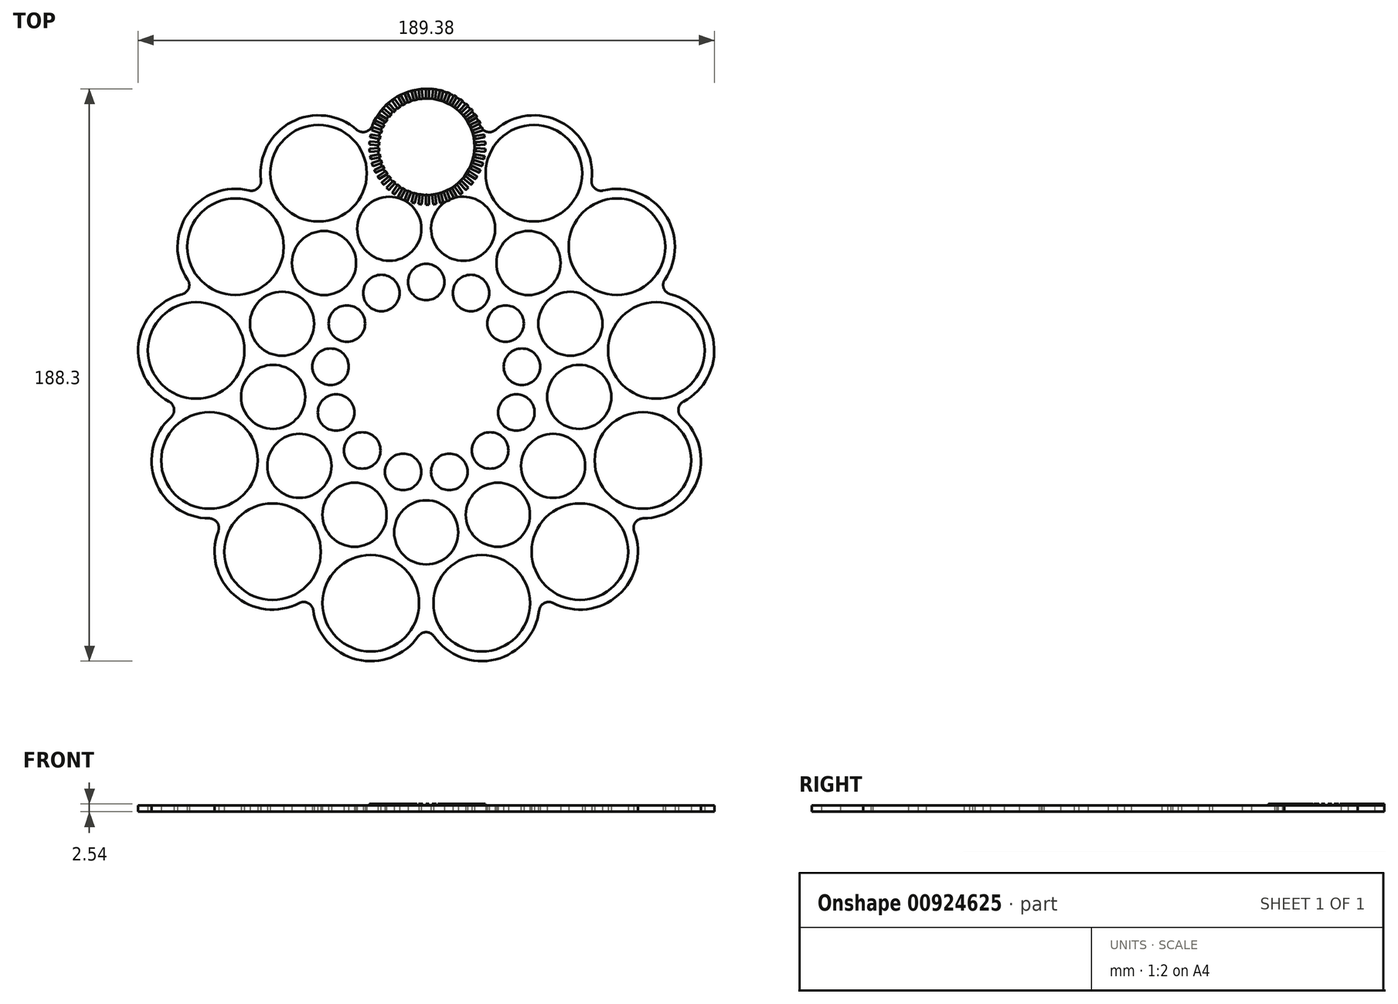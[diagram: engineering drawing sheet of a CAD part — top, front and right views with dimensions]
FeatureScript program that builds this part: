
annotation { "Feature Type Name" : "Feature", "Feature Type Description" : "" }
export const myFeature = defineFeature(function(context is Context, id is Id, definition is map)
    precondition{}
    {
        {
            var Q0;
            Q0=qCreatedBy(makeId("Top.planeOp"),FACE);
            var sketch = newSketch(context, id + "F0", { "sketchPlane" : qUnion([Q0])});
            skLineSegment(sketch, "E0", {"start": v(0, 0) * mm, "end": v(0, 76.2) * mm, "construction": true});
            skCircle(sketch, "E1", {"center": v(0, 76.2) * mm, "radius": 15.88 * mm});
            skLineSegment(sketch, "E2", {"start": v(0, 95.25) * mm, "end": v(0, 15.88) * mm, "construction": true});
            skCircle(sketch, "E3.1.0", {"center": v(-35.41, 67.47) * mm, "radius": 15.88 * mm});
            skArc(sketch, "E3.1.1", {"start": v(-22.84, 81.79) * mm, "mid": v(-44.26, 84.34) * mm, "end": v(-54.33, 65.26) * mm});
            skCircle(sketch, "E3.2.0", {"center": v(-62.71, 43.29) * mm, "radius": 15.88 * mm});
            skArc(sketch, "E3.2.1", {"start": v(-58.23, 61.8) * mm, "mid": v(-78.39, 54.1) * mm, "end": v(-78.44, 32.53) * mm});
            skCircle(sketch, "E3.3.0", {"center": v(-75.64, 9.18) * mm, "radius": 15.88 * mm});
            skArc(sketch, "E3.3.1", {"start": v(-80.28, 27.66) * mm, "mid": v(-94.56, 11.48) * mm, "end": v(-84.57, -7.64) * mm});
            skCircle(sketch, "E3.4.0", {"center": v(-71.25, -27.02) * mm, "radius": 15.88 * mm});
            skArc(sketch, "E3.4.1", {"start": v(-83.94, -12.82) * mm, "mid": v(-89.06, -33.78) * mm, "end": v(-71.33, -46.07) * mm});
            skCircle(sketch, "E3.5.0", {"center": v(-50.53, -57.04) * mm, "radius": 15.88 * mm});
            skArc(sketch, "E3.5.1", {"start": v(-68.37, -50.36) * mm, "mid": v(-63.16, -71.3) * mm, "end": v(-41.75, -73.94) * mm});
            skCircle(sketch, "E3.6.0", {"center": v(-18.24, -73.99) * mm, "radius": 15.88 * mm});
            skArc(sketch, "E3.6.1", {"start": v(-37.14, -76.36) * mm, "mid": v(-22.8, -92.48) * mm, "end": v(-2.6, -84.88) * mm});
            skCircle(sketch, "E3.7.0", {"center": v(18.24, -73.99) * mm, "radius": 15.88 * mm});
            skArc(sketch, "E3.7.1", {"start": v(2.6, -84.88) * mm, "mid": v(22.8, -92.48) * mm, "end": v(37.14, -76.36) * mm});
            skCircle(sketch, "E3.8.0", {"center": v(50.53, -57.04) * mm, "radius": 15.88 * mm});
            skArc(sketch, "E3.8.1", {"start": v(41.75, -73.94) * mm, "mid": v(63.16, -71.3) * mm, "end": v(68.37, -50.36) * mm});
            skCircle(sketch, "E3.9.0", {"center": v(71.25, -27.02) * mm, "radius": 15.88 * mm});
            skCircle(sketch, "E3.10.0", {"center": v(75.64, 9.18) * mm, "radius": 15.88 * mm});
            skArc(sketch, "E3.10.1", {"start": v(84.57, -7.64) * mm, "mid": v(94.56, 11.48) * mm, "end": v(80.28, 27.66) * mm});
            skCircle(sketch, "E3.11.0", {"center": v(62.71, 43.29) * mm, "radius": 15.88 * mm});
            skArc(sketch, "E3.11.1", {"start": v(78.44, 32.53) * mm, "mid": v(78.39, 54.1) * mm, "end": v(58.23, 61.8) * mm});
            skCircle(sketch, "E3.12.0", {"center": v(35.41, 67.47) * mm, "radius": 15.88 * mm});
            skPoint(sketch, "E3.center", {"position": v(0, 0) * mm});
            skLineSegment(sketch, "E4", {"start": v(0, 0) * mm, "end": v(35.41, 67.47) * mm, "construction": true});
            skLineSegment(sketch, "E5.0", {"start": v(-1.59, 0) * mm, "end": v(-1.59, 76.2) * mm, "construction": true});
            skLineSegment(sketch, "E6.0", {"start": v(1.4, -0.74) * mm, "end": v(36.82, 66.73) * mm, "construction": true});
            skCircle(sketch, "E7.0", {"center": v(12.13, 49.2) * mm, "radius": 10.54 * mm});
            skCircle(sketch, "E8.1.0", {"center": v(-12.13, 49.2) * mm, "radius": 10.54 * mm});
            skCircle(sketch, "E8.2.0", {"center": v(-33.6, 37.94) * mm, "radius": 10.54 * mm});
            skCircle(sketch, "E8.3.0", {"center": v(-47.39, 17.97) * mm, "radius": 10.54 * mm});
            skCircle(sketch, "E8.4.0", {"center": v(-50.31, -6.1) * mm, "radius": 10.54 * mm});
            skCircle(sketch, "E8.5.0", {"center": v(-41.7, -28.8) * mm, "radius": 10.54 * mm});
            skCircle(sketch, "E8.6.0", {"center": v(-23.55, -44.88) * mm, "radius": 10.54 * mm});
            skCircle(sketch, "E8.7.0", {"center": v(0, -50.68) * mm, "radius": 10.54 * mm});
            skCircle(sketch, "E8.8.0", {"center": v(23.55, -44.88) * mm, "radius": 10.54 * mm});
            skCircle(sketch, "E8.9.0", {"center": v(41.7, -28.8) * mm, "radius": 10.54 * mm});
            skCircle(sketch, "E8.10.0", {"center": v(50.31, -6.1) * mm, "radius": 10.54 * mm});
            skCircle(sketch, "E8.11.0", {"center": v(47.39, 17.97) * mm, "radius": 10.54 * mm});
            skCircle(sketch, "E8.12.0", {"center": v(33.6, 37.94) * mm, "radius": 10.54 * mm});
            skLineSegment(sketch, "E9", {"start": v(12.13, 49.2) * mm, "end": v(0, 0) * mm, "construction": true});
            skArc(sketch, "E10.trimOffspring", {"start": v(17.78, 83.03) * mm, "mid": v(0, 95.25) * mm, "end": v(-17.78, 83.03) * mm});
            skArc(sketch, "E11.trimOffspring", {"start": v(54.33, 65.26) * mm, "mid": v(44.26, 84.34) * mm, "end": v(22.84, 81.79) * mm});
            skCircle(sketch, "E12.0", {"center": v(0, 31.7) * mm, "radius": 6 * mm});
            skCircle(sketch, "E13.1.0", {"center": v(-14.73, 28.07) * mm, "radius": 6 * mm});
            skCircle(sketch, "E13.2.0", {"center": v(-26.09, 18) * mm, "radius": 6 * mm});
            skCircle(sketch, "E13.3.0", {"center": v(-31.47, 3.82) * mm, "radius": 6 * mm});
            skCircle(sketch, "E13.4.0", {"center": v(-29.64, -11.24) * mm, "radius": 6 * mm});
            skCircle(sketch, "E13.5.0", {"center": v(-21.02, -23.73) * mm, "radius": 6 * mm});
            skCircle(sketch, "E13.6.0", {"center": v(-7.59, -30.78) * mm, "radius": 6 * mm});
            skCircle(sketch, "E13.7.0", {"center": v(7.59, -30.78) * mm, "radius": 6 * mm});
            skCircle(sketch, "E13.8.0", {"center": v(21.02, -23.73) * mm, "radius": 6 * mm});
            skCircle(sketch, "E13.9.0", {"center": v(29.64, -11.24) * mm, "radius": 6 * mm});
            skCircle(sketch, "E13.10.0", {"center": v(31.47, 3.82) * mm, "radius": 6 * mm});
            skCircle(sketch, "E13.11.0", {"center": v(26.09, 18) * mm, "radius": 6 * mm});
            skCircle(sketch, "E13.12.0", {"center": v(14.73, 28.07) * mm, "radius": 6 * mm});
            skArc(sketch, "E14.trimOffspring", {"start": v(71.33, -46.07) * mm, "mid": v(89.06, -33.78) * mm, "end": v(83.94, -12.82) * mm});
            skPoint(sketch, "E15.visualSharp", {"position": v(-52.72, 59.5) * mm});
            skArc(sketch, "E15.filletArc", {"start": v(-58.23, 61.8) * mm, "mid": v(-55.38, 62.51) * mm, "end": v(-54.33, 65.26) * mm});
            skPoint(sketch, "E16.visualSharp", {"position": v(-74.33, 28.19) * mm});
            skArc(sketch, "E16.filletArc", {"start": v(-80.28, 27.66) * mm, "mid": v(-78.09, 29.61) * mm, "end": v(-78.44, 32.53) * mm});
            skPoint(sketch, "E17.visualSharp", {"position": v(-78.92, -9.58) * mm});
            skArc(sketch, "E17.filletArc", {"start": v(-83.94, -12.82) * mm, "mid": v(-82.9, -10.07) * mm, "end": v(-84.57, -7.64) * mm});
            skPoint(sketch, "E18.visualSharp", {"position": v(-65.42, -45.16) * mm});
            skArc(sketch, "E18.filletArc", {"start": v(-68.37, -50.36) * mm, "mid": v(-68.73, -47.44) * mm, "end": v(-71.33, -46.07) * mm});
            skPoint(sketch, "E19.visualSharp", {"position": v(-36.94, -70.39) * mm});
            skArc(sketch, "E19.filletArc", {"start": v(-37.14, -76.36) * mm, "mid": v(-38.81, -73.95) * mm, "end": v(-41.75, -73.94) * mm});
            skPoint(sketch, "E20.visualSharp", {"position": v(0, -79.5) * mm});
            skArc(sketch, "E20.filletArc", {"start": v(2.6, -84.88) * mm, "mid": v(0, -83.52) * mm, "end": v(-2.6, -84.88) * mm});
            skPoint(sketch, "E21.visualSharp", {"position": v(36.94, -70.39) * mm});
            skArc(sketch, "E21.filletArc", {"start": v(41.75, -73.94) * mm, "mid": v(38.81, -73.95) * mm, "end": v(37.14, -76.36) * mm});
            skPoint(sketch, "E22.visualSharp", {"position": v(65.42, -45.16) * mm});
            skArc(sketch, "E22.filletArc", {"start": v(71.33, -46.07) * mm, "mid": v(68.73, -47.44) * mm, "end": v(68.37, -50.36) * mm});
            skPoint(sketch, "E23.visualSharp", {"position": v(78.92, -9.58) * mm});
            skArc(sketch, "E23.filletArc", {"start": v(84.57, -7.64) * mm, "mid": v(82.9, -10.07) * mm, "end": v(83.94, -12.82) * mm});
            skPoint(sketch, "E24.visualSharp", {"position": v(74.33, 28.19) * mm});
            skArc(sketch, "E24.filletArc", {"start": v(78.44, 32.53) * mm, "mid": v(78.09, 29.61) * mm, "end": v(80.28, 27.66) * mm});
            skPoint(sketch, "E25.visualSharp", {"position": v(52.72, 59.5) * mm});
            skArc(sketch, "E25.filletArc", {"start": v(54.33, 65.26) * mm, "mid": v(55.38, 62.51) * mm, "end": v(58.23, 61.8) * mm});
            skPoint(sketch, "E26.visualSharp", {"position": v(19.02, 77.19) * mm});
            skArc(sketch, "E26.filletArc", {"start": v(17.78, 83.03) * mm, "mid": v(19.99, 81.09) * mm, "end": v(22.84, 81.79) * mm});
            skPoint(sketch, "E27.visualSharp", {"position": v(-19.02, 77.19) * mm});
            skArc(sketch, "E27.filletArc", {"start": v(-22.84, 81.79) * mm, "mid": v(-19.99, 81.09) * mm, "end": v(-17.78, 83.03) * mm});
            skSolve(sketch);
        }
        {
            var Q0;
            Q0 = qSketchRegion(id + "F0", true);
            extrude(context, id + "F1", {"entities" : qUnion([Q0]), "depth" : 2.03 * mm, "offsetDistance" : 25.4 * mm});
        }
        {
            var Q0;
            Q0=makeQuery(id+"F1.opExtrude","CAP_FACE",FACE,{"disambiguationData":[OSD([sQuery(id+"F0.wireOp",EDGE,"PSAwym5H-QxkA-4yG9-N3LV-itEtamM54euJ"),sQuery(id+"F0.wireOp",EDGE,"xVTmrC7g-0ckz-Fa8x-Pjiv-ewgNsUpUR1TQ"),sQuery(id+"F0.wireOp",EDGE,"E1"),sQuery(id+"F0.wireOp",EDGE,"fK0bV1JR-EDHa-cPX2-9ya8-nsOdXMEwq4Jo"),sQuery(id+"F0.wireOp",EDGE,"c6219e1f-16d4-4bd9-93b5-d01c4ede8f85"),sQuery(id+"F0.wireOp",EDGE,"f72ceaee-ed20-4dc2-a844-dc1204d0d60d.trimOffspring"),sQuery(id+"F0.wireOp",EDGE,"bad8b10d-c7dc-4f17-be22-73a892854aa8.trimOffspring"),sQuery(id+"F0.wireOp",EDGE,"7017c75f-0572-4b0f-bba0-e0d1ac50efab.trimOffspring"),sQuery(id+"F0.wireOp",EDGE,"a2bf4c4b-1b04-41ae-a137-ce36847d082b.filletArc"),sQuery(id+"F0.wireOp",EDGE,"9a5818be-14a7-4684-8801-1bcc1c34eb4a.filletArc"),sQuery(id+"F0.wireOp",EDGE,"76f430f3-cf00-46af-aaf1-ca3324483fb8.filletArc"),sQuery(id+"F0.wireOp",EDGE,"f2824564-7fb7-4ffd-9573-8c77cc779830.filletArc"),sQuery(id+"F0.wireOp",EDGE,"6882c2d4-6085-444e-aa9e-9cba060f5f8f.filletArc"),sQuery(id+"F0.wireOp",EDGE,"d489b73e-8a5e-456b-afac-9e78a89a280e.filletArc"),sQuery(id+"F0.wireOp",EDGE,"7932d08e-b7d8-4a8b-9c19-5e9f429760f1.trimOffspring"),sQuery(id+"F0.wireOp",EDGE,"vGADDeQr-Uufc-AQag-ZwEX-BwhNSN2T0gA2"),sQuery(id+"F0.wireOp",EDGE,"5JA08mAS-do2W-TdYA-RMZA-uYhekkPeP3UP")])],"isStart":false});
            var sketch = newSketch(context, id + "F2", { "sketchPlane" : qUnion([Q0])});
            skLineSegment(sketch, "E28", {"start": v(0.39, 95.26) * mm, "end": v(0.39, 92.07) * mm, "construction": true});
            skLineSegment(sketch, "E29.0", {"start": v(-0.12, 95.26) * mm, "end": v(-0.12, 92.07) * mm});
            skLineSegment(sketch, "E30", {"start": v(0.9, 95.25) * mm, "end": v(0.9, 92.05) * mm});
            skArc(sketch, "E31.0", {"start": v(0.9, 95.25) * mm, "mid": v(0.39, 95.26) * mm, "end": v(-0.12, 95.25) * mm});
            skArc(sketch, "E32.0", {"start": v(0.9, 92.05) * mm, "mid": v(0.39, 92.07) * mm, "end": v(-0.12, 92.07) * mm});
            skPoint(sketch, "E33.orphan", {"position": v(-12.06, 61.79) * mm});
            skPoint(sketch, "E34.orphan", {"position": v(12.84, 61.79) * mm});
            skLineSegment(sketch, "E35.1.0", {"start": v(-2.5, 95.04) * mm, "end": v(-2.1, 91.89) * mm});
            skLineSegment(sketch, "E35.1.1", {"start": v(-1.5, 95.16) * mm, "end": v(-1.1, 91.99) * mm});
            skLineSegment(sketch, "E35.1.2", {"start": v(-2, 95.1) * mm, "end": v(-1.6, 91.95) * mm, "construction": true});
            skArc(sketch, "E35.1.3", {"start": v(-1.1, 91.99) * mm, "mid": v(-1.6, 91.95) * mm, "end": v(-2.1, 91.89) * mm});
            skArc(sketch, "E35.1.4", {"start": v(-1.5, 95.16) * mm, "mid": v(-2, 95.1) * mm, "end": v(-2.5, 95.04) * mm});
            skLineSegment(sketch, "E35.2.0", {"start": v(-4.84, 94.53) * mm, "end": v(-4.05, 91.45) * mm});
            skLineSegment(sketch, "E35.2.1", {"start": v(-3.86, 94.78) * mm, "end": v(-3.06, 91.68) * mm});
            skLineSegment(sketch, "E35.2.2", {"start": v(-4.35, 94.66) * mm, "end": v(-3.56, 91.57) * mm, "construction": true});
            skArc(sketch, "E35.2.3", {"start": v(-3.06, 91.68) * mm, "mid": v(-3.56, 91.57) * mm, "end": v(-4.05, 91.45) * mm});
            skArc(sketch, "E35.2.4", {"start": v(-3.86, 94.78) * mm, "mid": v(-4.35, 94.66) * mm, "end": v(-4.84, 94.53) * mm});
            skLineSegment(sketch, "E35.3.0", {"start": v(-7.1, 93.73) * mm, "end": v(-5.93, 90.77) * mm});
            skLineSegment(sketch, "E35.3.1", {"start": v(-6.15, 94.1) * mm, "end": v(-4.97, 91.12) * mm});
            skLineSegment(sketch, "E35.3.2", {"start": v(-6.63, 93.92) * mm, "end": v(-5.45, 90.96) * mm, "construction": true});
            skArc(sketch, "E35.3.3", {"start": v(-4.97, 91.12) * mm, "mid": v(-5.45, 90.96) * mm, "end": v(-5.93, 90.77) * mm});
            skArc(sketch, "E35.3.4", {"start": v(-6.15, 94.1) * mm, "mid": v(-6.63, 93.92) * mm, "end": v(-7.1, 93.73) * mm});
            skLineSegment(sketch, "E35.4.0", {"start": v(-9.24, 92.66) * mm, "end": v(-7.7, 89.87) * mm});
            skLineSegment(sketch, "E35.4.1", {"start": v(-8.34, 93.14) * mm, "end": v(-6.8, 90.33) * mm});
            skLineSegment(sketch, "E35.4.2", {"start": v(-8.8, 92.9) * mm, "end": v(-7.25, 90.1) * mm, "construction": true});
            skArc(sketch, "E35.4.3", {"start": v(-6.8, 90.33) * mm, "mid": v(-7.25, 90.1) * mm, "end": v(-7.7, 89.87) * mm});
            skArc(sketch, "E35.4.4", {"start": v(-8.34, 93.14) * mm, "mid": v(-8.8, 92.9) * mm, "end": v(-9.23, 92.65) * mm});
            skLineSegment(sketch, "E35.5.0", {"start": v(-11.22, 91.32) * mm, "end": v(-9.35, 88.75) * mm});
            skLineSegment(sketch, "E35.5.1", {"start": v(-10.4, 91.91) * mm, "end": v(-8.51, 89.32) * mm});
            skLineSegment(sketch, "E35.5.2", {"start": v(-10.81, 91.62) * mm, "end": v(-8.94, 89.04) * mm, "construction": true});
            skArc(sketch, "E35.5.3", {"start": v(-8.51, 89.32) * mm, "mid": v(-8.94, 89.04) * mm, "end": v(-9.35, 88.75) * mm});
            skArc(sketch, "E35.5.4", {"start": v(-10.4, 91.91) * mm, "mid": v(-10.81, 91.62) * mm, "end": v(-11.22, 91.32) * mm});
            skLineSegment(sketch, "E35.6.0", {"start": v(-13.02, 89.75) * mm, "end": v(-10.84, 87.43) * mm});
            skLineSegment(sketch, "E35.6.1", {"start": v(-12.28, 90.44) * mm, "end": v(-10.09, 88.1) * mm});
            skLineSegment(sketch, "E35.6.2", {"start": v(-12.65, 90.1) * mm, "end": v(-10.47, 87.77) * mm, "construction": true});
            skArc(sketch, "E35.6.3", {"start": v(-10.09, 88.1) * mm, "mid": v(-10.47, 87.77) * mm, "end": v(-10.84, 87.43) * mm});
            skArc(sketch, "E35.6.4", {"start": v(-12.28, 90.44) * mm, "mid": v(-12.65, 90.1) * mm, "end": v(-13.02, 89.74) * mm});
            skLineSegment(sketch, "E35.7.0", {"start": v(-14.62, 87.96) * mm, "end": v(-12.16, 85.93) * mm});
            skLineSegment(sketch, "E35.7.1", {"start": v(-13.96, 88.74) * mm, "end": v(-11.5, 86.7) * mm});
            skLineSegment(sketch, "E35.7.2", {"start": v(-14.3, 88.35) * mm, "end": v(-11.84, 86.32) * mm, "construction": true});
            skArc(sketch, "E35.7.3", {"start": v(-11.5, 86.7) * mm, "mid": v(-11.84, 86.32) * mm, "end": v(-12.16, 85.93) * mm});
            skArc(sketch, "E35.7.4", {"start": v(-13.96, 88.74) * mm, "mid": v(-14.3, 88.35) * mm, "end": v(-14.6, 87.95) * mm});
            skLineSegment(sketch, "E35.8.0", {"start": v(-15.97, 85.99) * mm, "end": v(-13.28, 84.28) * mm});
            skLineSegment(sketch, "E35.8.1", {"start": v(-15.42, 86.84) * mm, "end": v(-12.72, 85.13) * mm});
            skLineSegment(sketch, "E35.8.2", {"start": v(-15.7, 86.42) * mm, "end": v(-13, 84.7) * mm, "construction": true});
            skArc(sketch, "E35.8.3", {"start": v(-12.72, 85.13) * mm, "mid": v(-13, 84.7) * mm, "end": v(-13.28, 84.28) * mm});
            skArc(sketch, "E35.8.4", {"start": v(-15.42, 86.84) * mm, "mid": v(-15.7, 86.42) * mm, "end": v(-15.96, 85.98) * mm});
            skLineSegment(sketch, "E35.9.0", {"start": v(-17.07, 83.86) * mm, "end": v(-14.19, 82.5) * mm});
            skLineSegment(sketch, "E35.9.1", {"start": v(-16.63, 84.78) * mm, "end": v(-13.73, 83.41) * mm});
            skLineSegment(sketch, "E35.9.2", {"start": v(-16.85, 84.32) * mm, "end": v(-13.97, 82.96) * mm, "construction": true});
            skArc(sketch, "E35.9.3", {"start": v(-13.73, 83.41) * mm, "mid": v(-13.97, 82.96) * mm, "end": v(-14.19, 82.5) * mm});
            skArc(sketch, "E35.9.4", {"start": v(-16.63, 84.78) * mm, "mid": v(-16.85, 84.32) * mm, "end": v(-17.06, 83.86) * mm});
            skLineSegment(sketch, "E35.10.0", {"start": v(-17.89, 81.61) * mm, "end": v(-14.86, 80.63) * mm});
            skLineSegment(sketch, "E35.10.1", {"start": v(-17.57, 82.58) * mm, "end": v(-14.52, 81.59) * mm});
            skLineSegment(sketch, "E35.10.2", {"start": v(-17.73, 82.1) * mm, "end": v(-14.7, 81.1) * mm, "construction": true});
            skArc(sketch, "E35.10.3", {"start": v(-14.52, 81.59) * mm, "mid": v(-14.7, 81.1) * mm, "end": v(-14.86, 80.63) * mm});
            skArc(sketch, "E35.10.4", {"start": v(-17.57, 82.58) * mm, "mid": v(-17.73, 82.1) * mm, "end": v(-17.88, 81.6) * mm});
            skLineSegment(sketch, "E35.11.0", {"start": v(-18.42, 79.28) * mm, "end": v(-15.3, 78.68) * mm});
            skLineSegment(sketch, "E35.11.1", {"start": v(-18.22, 80.28) * mm, "end": v(-15.08, 79.68) * mm});
            skLineSegment(sketch, "E35.11.2", {"start": v(-18.33, 79.78) * mm, "end": v(-15.2, 79.18) * mm, "construction": true});
            skArc(sketch, "E35.11.3", {"start": v(-15.08, 79.68) * mm, "mid": v(-15.2, 79.18) * mm, "end": v(-15.3, 78.68) * mm});
            skArc(sketch, "E35.11.4", {"start": v(-18.22, 80.28) * mm, "mid": v(-18.33, 79.78) * mm, "end": v(-18.41, 79.28) * mm});
            skLineSegment(sketch, "E35.12.0", {"start": v(-18.66, 76.9) * mm, "end": v(-15.48, 76.7) * mm});
            skLineSegment(sketch, "E35.12.1", {"start": v(-18.59, 77.91) * mm, "end": v(-15.4, 77.7) * mm});
            skLineSegment(sketch, "E35.12.2", {"start": v(-18.63, 77.4) * mm, "end": v(-15.44, 77.2) * mm, "construction": true});
            skArc(sketch, "E35.12.3", {"start": v(-15.4, 77.7) * mm, "mid": v(-15.44, 77.2) * mm, "end": v(-15.48, 76.7) * mm});
            skArc(sketch, "E35.12.4", {"start": v(-18.59, 77.91) * mm, "mid": v(-18.63, 77.4) * mm, "end": v(-18.65, 76.9) * mm});
            skLineSegment(sketch, "E35.13.0", {"start": v(-18.6, 74.5) * mm, "end": v(-15.42, 74.7) * mm});
            skLineSegment(sketch, "E35.13.1", {"start": v(-18.65, 75.52) * mm, "end": v(-15.46, 75.72) * mm});
            skLineSegment(sketch, "E35.13.2", {"start": v(-18.63, 75.01) * mm, "end": v(-15.44, 75.21) * mm, "construction": true});
            skArc(sketch, "E35.13.3", {"start": v(-15.46, 75.72) * mm, "mid": v(-15.44, 75.21) * mm, "end": v(-15.42, 74.7) * mm});
            skArc(sketch, "E35.13.4", {"start": v(-18.65, 75.52) * mm, "mid": v(-18.63, 75.01) * mm, "end": v(-18.59, 74.5) * mm});
            skLineSegment(sketch, "E35.14.0", {"start": v(-18.23, 72.14) * mm, "end": v(-15.1, 72.74) * mm});
            skLineSegment(sketch, "E35.14.1", {"start": v(-18.41, 73.14) * mm, "end": v(-15.27, 73.74) * mm});
            skLineSegment(sketch, "E35.14.2", {"start": v(-18.33, 72.64) * mm, "end": v(-15.2, 73.24) * mm, "construction": true});
            skArc(sketch, "E35.14.3", {"start": v(-15.27, 73.74) * mm, "mid": v(-15.2, 73.24) * mm, "end": v(-15.1, 72.74) * mm});
            skArc(sketch, "E35.14.4", {"start": v(-18.41, 73.14) * mm, "mid": v(-18.33, 72.64) * mm, "end": v(-18.22, 72.14) * mm});
            skLineSegment(sketch, "E35.15.0", {"start": v(-17.57, 69.84) * mm, "end": v(-14.55, 70.82) * mm});
            skLineSegment(sketch, "E35.15.1", {"start": v(-17.88, 70.8) * mm, "end": v(-14.84, 71.8) * mm});
            skLineSegment(sketch, "E35.15.2", {"start": v(-17.73, 70.32) * mm, "end": v(-14.7, 71.3) * mm, "construction": true});
            skArc(sketch, "E35.15.3", {"start": v(-14.84, 71.8) * mm, "mid": v(-14.7, 71.3) * mm, "end": v(-14.55, 70.82) * mm});
            skArc(sketch, "E35.15.4", {"start": v(-17.88, 70.8) * mm, "mid": v(-17.73, 70.32) * mm, "end": v(-17.57, 69.84) * mm});
            skLineSegment(sketch, "E35.16.0", {"start": v(-16.63, 67.64) * mm, "end": v(-13.75, 69) * mm});
            skLineSegment(sketch, "E35.16.1", {"start": v(-17.06, 68.56) * mm, "end": v(-14.16, 69.92) * mm});
            skLineSegment(sketch, "E35.16.2", {"start": v(-16.85, 68.1) * mm, "end": v(-13.97, 69.45) * mm, "construction": true});
            skArc(sketch, "E35.16.3", {"start": v(-14.16, 69.92) * mm, "mid": v(-13.97, 69.45) * mm, "end": v(-13.75, 69) * mm});
            skArc(sketch, "E35.16.4", {"start": v(-17.06, 68.56) * mm, "mid": v(-16.85, 68.1) * mm, "end": v(-16.63, 67.64) * mm});
            skLineSegment(sketch, "E35.17.0", {"start": v(-15.43, 65.57) * mm, "end": v(-12.74, 67.28) * mm});
            skLineSegment(sketch, "E35.17.1", {"start": v(-15.96, 66.43) * mm, "end": v(-13.26, 68.15) * mm});
            skLineSegment(sketch, "E35.17.2", {"start": v(-15.7, 66) * mm, "end": v(-13, 67.7) * mm, "construction": true});
            skArc(sketch, "E35.17.3", {"start": v(-13.26, 68.15) * mm, "mid": v(-13, 67.7) * mm, "end": v(-12.74, 67.28) * mm});
            skArc(sketch, "E35.17.4", {"start": v(-15.96, 66.43) * mm, "mid": v(-15.7, 66) * mm, "end": v(-15.42, 65.57) * mm});
            skLineSegment(sketch, "E35.18.0", {"start": v(-13.97, 63.67) * mm, "end": v(-11.51, 65.7) * mm});
            skLineSegment(sketch, "E35.18.1", {"start": v(-14.6, 64.46) * mm, "end": v(-12.14, 66.5) * mm});
            skLineSegment(sketch, "E35.18.2", {"start": v(-14.3, 64.06) * mm, "end": v(-11.84, 66.1) * mm, "construction": true});
            skArc(sketch, "E35.18.3", {"start": v(-12.14, 66.5) * mm, "mid": v(-11.84, 66.1) * mm, "end": v(-11.51, 65.7) * mm});
            skArc(sketch, "E35.18.4", {"start": v(-14.6, 64.46) * mm, "mid": v(-14.3, 64.06) * mm, "end": v(-13.96, 63.68) * mm});
            skLineSegment(sketch, "E35.19.0", {"start": v(-12.28, 61.97) * mm, "end": v(-10.1, 64.3) * mm});
            skLineSegment(sketch, "E35.19.1", {"start": v(-13.02, 62.67) * mm, "end": v(-10.83, 65) * mm});
            skLineSegment(sketch, "E35.19.2", {"start": v(-12.65, 62.32) * mm, "end": v(-10.47, 64.64) * mm, "construction": true});
            skArc(sketch, "E35.19.3", {"start": v(-10.83, 65) * mm, "mid": v(-10.47, 64.64) * mm, "end": v(-10.1, 64.3) * mm});
            skArc(sketch, "E35.19.4", {"start": v(-13.02, 62.67) * mm, "mid": v(-12.65, 62.32) * mm, "end": v(-12.28, 61.98) * mm});
            skLineSegment(sketch, "E35.20.0", {"start": v(-10.4, 60.5) * mm, "end": v(-8.53, 63.07) * mm});
            skLineSegment(sketch, "E35.20.1", {"start": v(-11.22, 61.1) * mm, "end": v(-9.34, 63.69) * mm});
            skLineSegment(sketch, "E35.20.2", {"start": v(-10.81, 60.8) * mm, "end": v(-8.94, 63.37) * mm, "construction": true});
            skArc(sketch, "E35.20.3", {"start": v(-9.34, 63.69) * mm, "mid": v(-8.94, 63.37) * mm, "end": v(-8.53, 63.07) * mm});
            skArc(sketch, "E35.20.4", {"start": v(-11.22, 61.1) * mm, "mid": v(-10.81, 60.8) * mm, "end": v(-10.4, 60.5) * mm});
            skLineSegment(sketch, "E35.21.0", {"start": v(-8.35, 59.27) * mm, "end": v(-6.81, 62.06) * mm});
            skLineSegment(sketch, "E35.21.1", {"start": v(-9.23, 59.76) * mm, "end": v(-7.7, 62.57) * mm});
            skLineSegment(sketch, "E35.21.2", {"start": v(-8.8, 59.51) * mm, "end": v(-7.25, 62.3) * mm, "construction": true});
            skArc(sketch, "E35.21.3", {"start": v(-7.7, 62.57) * mm, "mid": v(-7.26, 62.3) * mm, "end": v(-6.81, 62.06) * mm});
            skArc(sketch, "E35.21.4", {"start": v(-9.23, 59.76) * mm, "mid": v(-8.8, 59.51) * mm, "end": v(-8.34, 59.28) * mm});
            skLineSegment(sketch, "E35.22.0", {"start": v(-6.15, 58.3) * mm, "end": v(-4.98, 61.27) * mm});
            skLineSegment(sketch, "E35.22.1", {"start": v(-7.1, 58.69) * mm, "end": v(-5.92, 61.67) * mm});
            skLineSegment(sketch, "E35.22.2", {"start": v(-6.63, 58.5) * mm, "end": v(-5.45, 61.46) * mm, "construction": true});
            skArc(sketch, "E35.22.3", {"start": v(-5.92, 61.67) * mm, "mid": v(-5.45, 61.46) * mm, "end": v(-4.98, 61.27) * mm});
            skArc(sketch, "E35.22.4", {"start": v(-7.1, 58.69) * mm, "mid": v(-6.63, 58.5) * mm, "end": v(-6.15, 58.31) * mm});
            skLineSegment(sketch, "E35.23.0", {"start": v(-3.86, 57.63) * mm, "end": v(-3.07, 60.71) * mm});
            skLineSegment(sketch, "E35.23.1", {"start": v(-4.84, 57.89) * mm, "end": v(-4.04, 60.99) * mm});
            skLineSegment(sketch, "E35.23.2", {"start": v(-4.35, 57.76) * mm, "end": v(-3.56, 60.84) * mm, "construction": true});
            skArc(sketch, "E35.23.3", {"start": v(-4.04, 60.99) * mm, "mid": v(-3.56, 60.84) * mm, "end": v(-3.07, 60.71) * mm});
            skArc(sketch, "E35.23.4", {"start": v(-4.84, 57.89) * mm, "mid": v(-4.35, 57.76) * mm, "end": v(-3.86, 57.64) * mm});
            skLineSegment(sketch, "E35.24.0", {"start": v(-1.5, 57.24) * mm, "end": v(-1.1, 60.4) * mm});
            skLineSegment(sketch, "E35.24.1", {"start": v(-2.5, 57.38) * mm, "end": v(-2.1, 60.55) * mm});
            skLineSegment(sketch, "E35.24.2", {"start": v(-2, 57.3) * mm, "end": v(-1.6, 60.47) * mm, "construction": true});
            skArc(sketch, "E35.24.3", {"start": v(-2.1, 60.55) * mm, "mid": v(-1.6, 60.47) * mm, "end": v(-1.1, 60.4) * mm});
            skArc(sketch, "E35.24.4", {"start": v(-2.5, 57.38) * mm, "mid": v(-2, 57.3) * mm, "end": v(-1.5, 57.25) * mm});
            skLineSegment(sketch, "E35.25.0", {"start": v(0.9, 57.16) * mm, "end": v(0.9, 60.34) * mm});
            skLineSegment(sketch, "E35.25.1", {"start": v(-0.12, 57.16) * mm, "end": v(-0.12, 60.37) * mm});
            skLineSegment(sketch, "E35.25.2", {"start": v(0.39, 57.16) * mm, "end": v(0.39, 60.35) * mm, "construction": true});
            skArc(sketch, "E35.25.3", {"start": v(-0.12, 60.37) * mm, "mid": v(0.39, 60.35) * mm, "end": v(0.9, 60.34) * mm});
            skArc(sketch, "E35.25.4", {"start": v(-0.12, 57.16) * mm, "mid": v(0.39, 57.16) * mm, "end": v(0.9, 57.16) * mm});
            skLineSegment(sketch, "E35.26.0", {"start": v(3.28, 57.37) * mm, "end": v(2.88, 60.53) * mm});
            skLineSegment(sketch, "E35.26.1", {"start": v(2.27, 57.25) * mm, "end": v(1.87, 60.43) * mm});
            skLineSegment(sketch, "E35.26.2", {"start": v(2.77, 57.3) * mm, "end": v(2.38, 60.47) * mm, "construction": true});
            skArc(sketch, "E35.26.3", {"start": v(1.87, 60.43) * mm, "mid": v(2.37, 60.47) * mm, "end": v(2.88, 60.53) * mm});
            skArc(sketch, "E35.26.4", {"start": v(2.27, 57.25) * mm, "mid": v(2.77, 57.3) * mm, "end": v(3.28, 57.38) * mm});
            skLineSegment(sketch, "E35.27.0", {"start": v(5.62, 57.88) * mm, "end": v(4.83, 60.97) * mm});
            skLineSegment(sketch, "E35.27.1", {"start": v(4.63, 57.64) * mm, "end": v(3.83, 60.74) * mm});
            skLineSegment(sketch, "E35.27.2", {"start": v(5.12, 57.76) * mm, "end": v(4.33, 60.84) * mm, "construction": true});
            skArc(sketch, "E35.27.3", {"start": v(3.83, 60.74) * mm, "mid": v(4.33, 60.84) * mm, "end": v(4.83, 60.97) * mm});
            skArc(sketch, "E35.27.4", {"start": v(4.63, 57.64) * mm, "mid": v(5.12, 57.76) * mm, "end": v(5.61, 57.89) * mm});
            skLineSegment(sketch, "E35.28.0", {"start": v(7.87, 58.68) * mm, "end": v(6.7, 61.64) * mm});
            skLineSegment(sketch, "E35.28.1", {"start": v(6.92, 58.31) * mm, "end": v(5.75, 61.3) * mm});
            skLineSegment(sketch, "E35.28.2", {"start": v(7.4, 58.5) * mm, "end": v(6.23, 61.46) * mm, "construction": true});
            skArc(sketch, "E35.28.3", {"start": v(5.75, 61.3) * mm, "mid": v(6.23, 61.46) * mm, "end": v(6.7, 61.64) * mm});
            skArc(sketch, "E35.28.4", {"start": v(6.92, 58.31) * mm, "mid": v(7.4, 58.5) * mm, "end": v(7.87, 58.69) * mm});
            skLineSegment(sketch, "E35.29.0", {"start": v(10, 59.76) * mm, "end": v(8.48, 62.55) * mm});
            skLineSegment(sketch, "E35.29.1", {"start": v(9.12, 59.28) * mm, "end": v(7.57, 62.08) * mm});
            skLineSegment(sketch, "E35.29.2", {"start": v(9.56, 59.51) * mm, "end": v(8.03, 62.3) * mm, "construction": true});
            skArc(sketch, "E35.29.3", {"start": v(7.57, 62.08) * mm, "mid": v(8.03, 62.3) * mm, "end": v(8.48, 62.55) * mm});
            skArc(sketch, "E35.29.4", {"start": v(9.12, 59.28) * mm, "mid": v(9.56, 59.51) * mm, "end": v(10, 59.76) * mm});
            skLineSegment(sketch, "E35.30.0", {"start": v(12, 61.1) * mm, "end": v(10.12, 63.67) * mm});
            skLineSegment(sketch, "E35.30.1", {"start": v(11.17, 60.5) * mm, "end": v(9.29, 63.1) * mm});
            skLineSegment(sketch, "E35.30.2", {"start": v(11.58, 60.8) * mm, "end": v(9.71, 63.37) * mm, "construction": true});
            skArc(sketch, "E35.30.3", {"start": v(9.29, 63.1) * mm, "mid": v(9.71, 63.37) * mm, "end": v(10.12, 63.67) * mm});
            skArc(sketch, "E35.30.4", {"start": v(11.17, 60.5) * mm, "mid": v(11.58, 60.8) * mm, "end": v(12, 61.1) * mm});
            skLineSegment(sketch, "E35.31.0", {"start": v(13.8, 62.67) * mm, "end": v(11.62, 64.99) * mm});
            skLineSegment(sketch, "E35.31.1", {"start": v(13.05, 61.98) * mm, "end": v(10.86, 64.31) * mm});
            skLineSegment(sketch, "E35.31.2", {"start": v(13.43, 62.32) * mm, "end": v(11.25, 64.64) * mm, "construction": true});
            skArc(sketch, "E35.31.3", {"start": v(10.86, 64.31) * mm, "mid": v(11.25, 64.64) * mm, "end": v(11.62, 64.99) * mm});
            skArc(sketch, "E35.31.4", {"start": v(13.05, 61.98) * mm, "mid": v(13.43, 62.32) * mm, "end": v(13.8, 62.67) * mm});
            skLineSegment(sketch, "E35.32.0", {"start": v(15.39, 64.46) * mm, "end": v(12.94, 66.49) * mm});
            skLineSegment(sketch, "E35.32.1", {"start": v(14.74, 63.68) * mm, "end": v(12.27, 65.72) * mm});
            skLineSegment(sketch, "E35.32.2", {"start": v(15.07, 64.06) * mm, "end": v(12.6, 66.1) * mm, "construction": true});
            skArc(sketch, "E35.32.3", {"start": v(12.27, 65.72) * mm, "mid": v(12.6, 66.1) * mm, "end": v(12.94, 66.49) * mm});
            skArc(sketch, "E35.32.4", {"start": v(14.74, 63.68) * mm, "mid": v(15.07, 64.06) * mm, "end": v(15.38, 64.46) * mm});
            skLineSegment(sketch, "E35.33.0", {"start": v(16.74, 66.43) * mm, "end": v(14.06, 68.13) * mm});
            skLineSegment(sketch, "E35.33.1", {"start": v(16.2, 65.57) * mm, "end": v(13.5, 67.3) * mm});
            skLineSegment(sketch, "E35.33.2", {"start": v(16.47, 66) * mm, "end": v(13.78, 67.7) * mm, "construction": true});
            skArc(sketch, "E35.33.3", {"start": v(13.5, 67.3) * mm, "mid": v(13.78, 67.7) * mm, "end": v(14.06, 68.13) * mm});
            skArc(sketch, "E35.33.4", {"start": v(16.2, 65.57) * mm, "mid": v(16.47, 66) * mm, "end": v(16.74, 66.43) * mm});
            skLineSegment(sketch, "E35.34.0", {"start": v(17.84, 68.56) * mm, "end": v(14.96, 69.91) * mm});
            skLineSegment(sketch, "E35.34.1", {"start": v(17.4, 67.64) * mm, "end": v(14.5, 69) * mm});
            skLineSegment(sketch, "E35.34.2", {"start": v(17.62, 68.1) * mm, "end": v(14.74, 69.45) * mm, "construction": true});
            skArc(sketch, "E35.34.3", {"start": v(14.5, 69) * mm, "mid": v(14.74, 69.45) * mm, "end": v(14.96, 69.91) * mm});
            skArc(sketch, "E35.34.4", {"start": v(17.4, 67.64) * mm, "mid": v(17.62, 68.1) * mm, "end": v(17.83, 68.56) * mm});
            skLineSegment(sketch, "E35.35.0", {"start": v(18.66, 70.8) * mm, "end": v(15.63, 71.79) * mm});
            skLineSegment(sketch, "E35.35.1", {"start": v(18.34, 69.84) * mm, "end": v(15.3, 70.83) * mm});
            skLineSegment(sketch, "E35.35.2", {"start": v(18.5, 70.32) * mm, "end": v(15.47, 71.3) * mm, "construction": true});
            skArc(sketch, "E35.35.3", {"start": v(15.3, 70.83) * mm, "mid": v(15.47, 71.3) * mm, "end": v(15.63, 71.79) * mm});
            skArc(sketch, "E35.35.4", {"start": v(18.34, 69.84) * mm, "mid": v(18.5, 70.32) * mm, "end": v(18.66, 70.8) * mm});
            skLineSegment(sketch, "E35.36.0", {"start": v(19.2, 73.14) * mm, "end": v(16.07, 73.73) * mm});
            skLineSegment(sketch, "E35.36.1", {"start": v(19, 72.14) * mm, "end": v(15.85, 72.74) * mm});
            skLineSegment(sketch, "E35.36.2", {"start": v(19.1, 72.64) * mm, "end": v(15.97, 73.24) * mm, "construction": true});
            skArc(sketch, "E35.36.3", {"start": v(15.85, 72.74) * mm, "mid": v(15.97, 73.24) * mm, "end": v(16.07, 73.73) * mm});
            skArc(sketch, "E35.36.4", {"start": v(19, 72.14) * mm, "mid": v(19.1, 72.64) * mm, "end": v(19.19, 73.14) * mm});
            skLineSegment(sketch, "E35.37.0", {"start": v(19.43, 75.52) * mm, "end": v(16.25, 75.72) * mm});
            skLineSegment(sketch, "E35.37.1", {"start": v(19.36, 74.5) * mm, "end": v(16.17, 74.7) * mm});
            skLineSegment(sketch, "E35.37.2", {"start": v(19.4, 75.01) * mm, "end": v(16.22, 75.21) * mm, "construction": true});
            skArc(sketch, "E35.37.3", {"start": v(16.17, 74.7) * mm, "mid": v(16.22, 75.21) * mm, "end": v(16.25, 75.72) * mm});
            skArc(sketch, "E35.37.4", {"start": v(19.36, 74.5) * mm, "mid": v(19.4, 75.01) * mm, "end": v(19.42, 75.52) * mm});
            skLineSegment(sketch, "E35.38.0", {"start": v(19.37, 77.91) * mm, "end": v(16.2, 77.71) * mm});
            skLineSegment(sketch, "E35.38.1", {"start": v(19.42, 76.9) * mm, "end": v(16.23, 76.7) * mm});
            skLineSegment(sketch, "E35.38.2", {"start": v(19.4, 77.4) * mm, "end": v(16.22, 77.2) * mm, "construction": true});
            skArc(sketch, "E35.38.3", {"start": v(16.23, 76.7) * mm, "mid": v(16.22, 77.2) * mm, "end": v(16.2, 77.71) * mm});
            skArc(sketch, "E35.38.4", {"start": v(19.42, 76.9) * mm, "mid": v(19.4, 77.4) * mm, "end": v(19.36, 77.91) * mm});
            skLineSegment(sketch, "E35.39.0", {"start": v(19, 80.28) * mm, "end": v(15.88, 79.68) * mm});
            skLineSegment(sketch, "E35.39.1", {"start": v(19.19, 79.28) * mm, "end": v(16.04, 78.68) * mm});
            skLineSegment(sketch, "E35.39.2", {"start": v(19.1, 79.78) * mm, "end": v(15.97, 79.18) * mm, "construction": true});
            skArc(sketch, "E35.39.3", {"start": v(16.04, 78.68) * mm, "mid": v(15.97, 79.18) * mm, "end": v(15.88, 79.68) * mm});
            skArc(sketch, "E35.39.4", {"start": v(19.19, 79.28) * mm, "mid": v(19.1, 79.78) * mm, "end": v(19, 80.28) * mm});
            skLineSegment(sketch, "E35.40.0", {"start": v(18.35, 82.58) * mm, "end": v(15.32, 81.6) * mm});
            skLineSegment(sketch, "E35.40.1", {"start": v(18.66, 81.6) * mm, "end": v(15.61, 80.62) * mm});
            skLineSegment(sketch, "E35.40.2", {"start": v(18.5, 82.1) * mm, "end": v(15.47, 81.1) * mm, "construction": true});
            skArc(sketch, "E35.40.3", {"start": v(15.61, 80.62) * mm, "mid": v(15.47, 81.1) * mm, "end": v(15.32, 81.6) * mm});
            skArc(sketch, "E35.40.4", {"start": v(18.66, 81.6) * mm, "mid": v(18.5, 82.1) * mm, "end": v(18.34, 82.58) * mm});
            skLineSegment(sketch, "E35.41.0", {"start": v(17.4, 84.78) * mm, "end": v(14.53, 83.42) * mm});
            skLineSegment(sketch, "E35.41.1", {"start": v(17.83, 83.86) * mm, "end": v(14.94, 82.5) * mm});
            skLineSegment(sketch, "E35.41.2", {"start": v(17.62, 84.32) * mm, "end": v(14.74, 82.96) * mm, "construction": true});
            skArc(sketch, "E35.41.3", {"start": v(14.94, 82.5) * mm, "mid": v(14.74, 82.96) * mm, "end": v(14.53, 83.42) * mm});
            skArc(sketch, "E35.41.4", {"start": v(17.83, 83.86) * mm, "mid": v(17.62, 84.32) * mm, "end": v(17.4, 84.78) * mm});
            skLineSegment(sketch, "E35.42.0", {"start": v(16.2, 86.84) * mm, "end": v(13.51, 85.14) * mm});
            skLineSegment(sketch, "E35.42.1", {"start": v(16.74, 85.98) * mm, "end": v(14.04, 84.27) * mm});
            skLineSegment(sketch, "E35.42.2", {"start": v(16.47, 86.42) * mm, "end": v(13.78, 84.7) * mm, "construction": true});
            skArc(sketch, "E35.42.3", {"start": v(14.04, 84.27) * mm, "mid": v(13.78, 84.7) * mm, "end": v(13.51, 85.14) * mm});
            skArc(sketch, "E35.42.4", {"start": v(16.74, 85.98) * mm, "mid": v(16.47, 86.42) * mm, "end": v(16.2, 86.84) * mm});
            skLineSegment(sketch, "E35.43.0", {"start": v(14.74, 88.74) * mm, "end": v(12.29, 86.71) * mm});
            skLineSegment(sketch, "E35.43.1", {"start": v(15.38, 87.95) * mm, "end": v(12.92, 85.91) * mm});
            skLineSegment(sketch, "E35.43.2", {"start": v(15.07, 88.35) * mm, "end": v(12.6, 86.32) * mm, "construction": true});
            skArc(sketch, "E35.43.3", {"start": v(12.92, 85.91) * mm, "mid": v(12.6, 86.32) * mm, "end": v(12.29, 86.71) * mm});
            skArc(sketch, "E35.43.4", {"start": v(15.38, 87.95) * mm, "mid": v(15.07, 88.35) * mm, "end": v(14.74, 88.74) * mm});
            skLineSegment(sketch, "E35.44.0", {"start": v(13.06, 90.44) * mm, "end": v(10.88, 88.12) * mm});
            skLineSegment(sketch, "E35.44.1", {"start": v(13.8, 89.74) * mm, "end": v(11.6, 87.4) * mm});
            skLineSegment(sketch, "E35.44.2", {"start": v(13.43, 90.1) * mm, "end": v(11.25, 87.77) * mm, "construction": true});
            skArc(sketch, "E35.44.3", {"start": v(11.6, 87.4) * mm, "mid": v(11.25, 87.77) * mm, "end": v(10.88, 88.12) * mm});
            skArc(sketch, "E35.44.4", {"start": v(13.8, 89.74) * mm, "mid": v(13.43, 90.1) * mm, "end": v(13.05, 90.44) * mm});
            skLineSegment(sketch, "E35.45.0", {"start": v(11.17, 91.92) * mm, "end": v(9.3, 89.34) * mm});
            skLineSegment(sketch, "E35.45.1", {"start": v(12, 91.32) * mm, "end": v(10.1, 88.73) * mm});
            skLineSegment(sketch, "E35.45.2", {"start": v(11.58, 91.62) * mm, "end": v(9.71, 89.04) * mm, "construction": true});
            skArc(sketch, "E35.45.3", {"start": v(10.1, 88.73) * mm, "mid": v(9.71, 89.04) * mm, "end": v(9.3, 89.34) * mm});
            skArc(sketch, "E35.45.4", {"start": v(12, 91.32) * mm, "mid": v(11.58, 91.62) * mm, "end": v(11.17, 91.91) * mm});
            skLineSegment(sketch, "E35.46.0", {"start": v(9.12, 93.15) * mm, "end": v(7.59, 90.36) * mm});
            skLineSegment(sketch, "E35.46.1", {"start": v(10, 92.65) * mm, "end": v(8.46, 89.85) * mm});
            skLineSegment(sketch, "E35.46.2", {"start": v(9.56, 92.9) * mm, "end": v(8.03, 90.1) * mm, "construction": true});
            skArc(sketch, "E35.46.3", {"start": v(8.46, 89.85) * mm, "mid": v(8.03, 90.1) * mm, "end": v(7.59, 90.36) * mm});
            skArc(sketch, "E35.46.4", {"start": v(10, 92.65) * mm, "mid": v(9.56, 92.9) * mm, "end": v(9.12, 93.14) * mm});
            skLineSegment(sketch, "E35.47.0", {"start": v(6.93, 94.1) * mm, "end": v(5.76, 91.15) * mm});
            skLineSegment(sketch, "E35.47.1", {"start": v(7.87, 93.73) * mm, "end": v(6.7, 90.75) * mm});
            skLineSegment(sketch, "E35.47.2", {"start": v(7.4, 93.92) * mm, "end": v(6.23, 90.96) * mm, "construction": true});
            skArc(sketch, "E35.47.3", {"start": v(6.7, 90.75) * mm, "mid": v(6.23, 90.96) * mm, "end": v(5.76, 91.15) * mm});
            skArc(sketch, "E35.47.4", {"start": v(7.87, 93.73) * mm, "mid": v(7.4, 93.92) * mm, "end": v(6.92, 94.1) * mm});
            skLineSegment(sketch, "E35.48.0", {"start": v(4.63, 94.79) * mm, "end": v(3.84, 91.7) * mm});
            skLineSegment(sketch, "E35.48.1", {"start": v(5.61, 94.53) * mm, "end": v(4.82, 91.43) * mm});
            skLineSegment(sketch, "E35.48.2", {"start": v(5.12, 94.66) * mm, "end": v(4.33, 91.57) * mm, "construction": true});
            skArc(sketch, "E35.48.3", {"start": v(4.82, 91.43) * mm, "mid": v(4.33, 91.57) * mm, "end": v(3.84, 91.7) * mm});
            skArc(sketch, "E35.48.4", {"start": v(5.61, 94.53) * mm, "mid": v(5.12, 94.66) * mm, "end": v(4.63, 94.78) * mm});
            skLineSegment(sketch, "E35.49.0", {"start": v(2.27, 95.17) * mm, "end": v(1.87, 92.01) * mm});
            skLineSegment(sketch, "E35.49.1", {"start": v(3.28, 95.04) * mm, "end": v(2.88, 91.86) * mm});
            skLineSegment(sketch, "E35.49.2", {"start": v(2.77, 95.1) * mm, "end": v(2.38, 91.95) * mm, "construction": true});
            skArc(sketch, "E35.49.3", {"start": v(2.88, 91.86) * mm, "mid": v(2.38, 91.95) * mm, "end": v(1.87, 92.01) * mm});
            skArc(sketch, "E35.49.4", {"start": v(3.28, 95.04) * mm, "mid": v(2.77, 95.1) * mm, "end": v(2.27, 95.16) * mm});
            skSolve(sketch);
        }
        {
            var Q0;
            Q0 = qSketchRegion(id + "F2", true);
            extrude(context, id + "F3", {"entities" : qUnion([Q0]), "operationType" : NewBodyOperationType.ADD, "depth" : 0.5 * mm, "offsetDistance" : 25.4 * mm});
        }
    });
